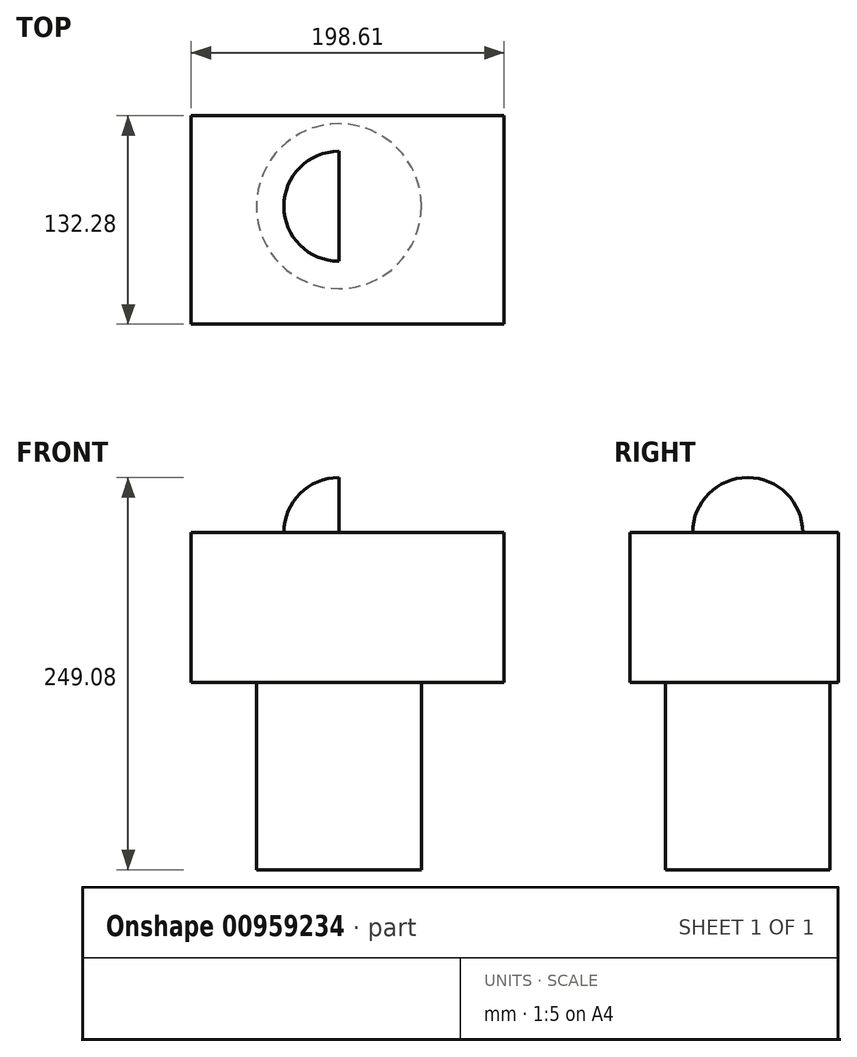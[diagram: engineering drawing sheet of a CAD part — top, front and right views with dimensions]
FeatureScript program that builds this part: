
annotation { "Feature Type Name" : "Feature", "Feature Type Description" : "" }
export const myFeature = defineFeature(function(context is Context, id is Id, definition is map)
    precondition{}
    {
        {
            var Q0;
            Q0=qCreatedBy(makeId("Top.planeOp"),FACE);
            var sketch = newSketch(context, id + "F0", { "sketchPlane" : qUnion([Q0])});
            skCircle(sketch, "E0", {"center": v(0, 0) * mm, "radius": 52.35 * mm});
            skSolve(sketch);
        }
        {
            var Q0;
            Q0=makeQuery(id+"F0.imprint","IMPRINT",FACE,{"disambiguationData":[TD([[makeQuery(id+"F0.imprint","IMPRINT",EDGE,{"derivedFrom":sQuery(id+"F0.wireOp",EDGE,"E0")}),1.0]])]});
            extrude(context, id + "F1", {"entities" : qUnion([Q0]), "depth" : 118.87 * mm, "offsetDistance" : 25.4 * mm});
        }
        {
            var Q0;
            Q0=makeQuery(id+"F1.opExtrude","CAP_FACE",FACE,{"disambiguationData":[OSD([sQuery(id+"F0.wireOp",EDGE,"E0")])],"isStart":false});
            var sketch = newSketch(context, id + "F2", { "sketchPlane" : qUnion([Q0])});
            skLineSegment(sketch, "E1.bottom", {"start": v(-93.77, 57.45) * mm, "end": v(104.84, 57.45) * mm});
            skLineSegment(sketch, "E1.top", {"start": v(-93.77, -74.83) * mm, "end": v(104.84, -74.83) * mm});
            skLineSegment(sketch, "E1.left", {"start": v(-93.77, 57.45) * mm, "end": v(-93.77, -74.83) * mm});
            skLineSegment(sketch, "E1.right", {"start": v(104.84, 57.45) * mm, "end": v(104.84, -74.83) * mm});
            skSolve(sketch);
        }
        {
            var Q0;
            Q0 = qSketchRegion(id + "F2", true);
            extrude(context, id + "F3", {"entities" : qUnion([Q0]), "operationType" : NewBodyOperationType.ADD, "depth" : 95.25 * mm, "offsetDistance" : 25.4 * mm});
        }
        {
            var Q0;
            Q0=makeQuery(id+"F3.opExtrude","CAP_FACE",FACE,{"disambiguationData":[OSD([sQuery(id+"F2.wireOp",EDGE,"E1.bottom"),sQuery(id+"F2.wireOp",EDGE,"E1.top"),sQuery(id+"F2.wireOp",EDGE,"E1.left"),sQuery(id+"F2.wireOp",EDGE,"E1.right")])],"isStart":false});
            var sketch = newSketch(context, id + "F4", { "sketchPlane" : qUnion([Q0])});
            skArc(sketch, "E2", {"start": v(0, 34.95) * mm, "mid": v(-34.95, 0) * mm, "end": v(0, -34.95) * mm});
            skLineSegment(sketch, "E3", {"start": v(0, 34.95) * mm, "end": v(0, -34.95) * mm});
            skSolve(sketch);
        }
        {
            var Q0;
            Q0=makeQuery(id+"F4.imprint","IMPRINT",FACE,{"disambiguationData":[TD([[makeQuery(id+"F4.imprint","IMPRINT",EDGE,{"derivedFrom":sQuery(id+"F4.wireOp",EDGE,"E2")}),1.0]])]});
            var Q1;
            Q1=sQuery(id+"F4.wireOp",EDGE,"E3");
            revolve(context, id + "F5", {"operationType" : NewBodyOperationType.ADD, "surfaceOperationType" : NewSurfaceOperationType.NEW, "entities" : qUnion([Q0]), "axis" : qUnion([Q1]), "revolveType" : RevolveType.SYMMETRIC, "oppositeDirection" : true, "angle" : 180 * degree});
        }
        {
            var Q0;
            Q0=makeQuery(id+"F3.opExtrude","SWEPT_FACE",FACE,{"disambiguationData":[OSD([sQuery(id+"F2.wireOp",EDGE,"E1.left")])]});
            cPlane(context, id + "F6", {"entities" : qUnion([Q0]), "cplaneType" : CPlaneType.OFFSET, "offset" : 127 * mm, "width" : 152.4 * mm, "height" : 152.4 * mm});
        }
    });
